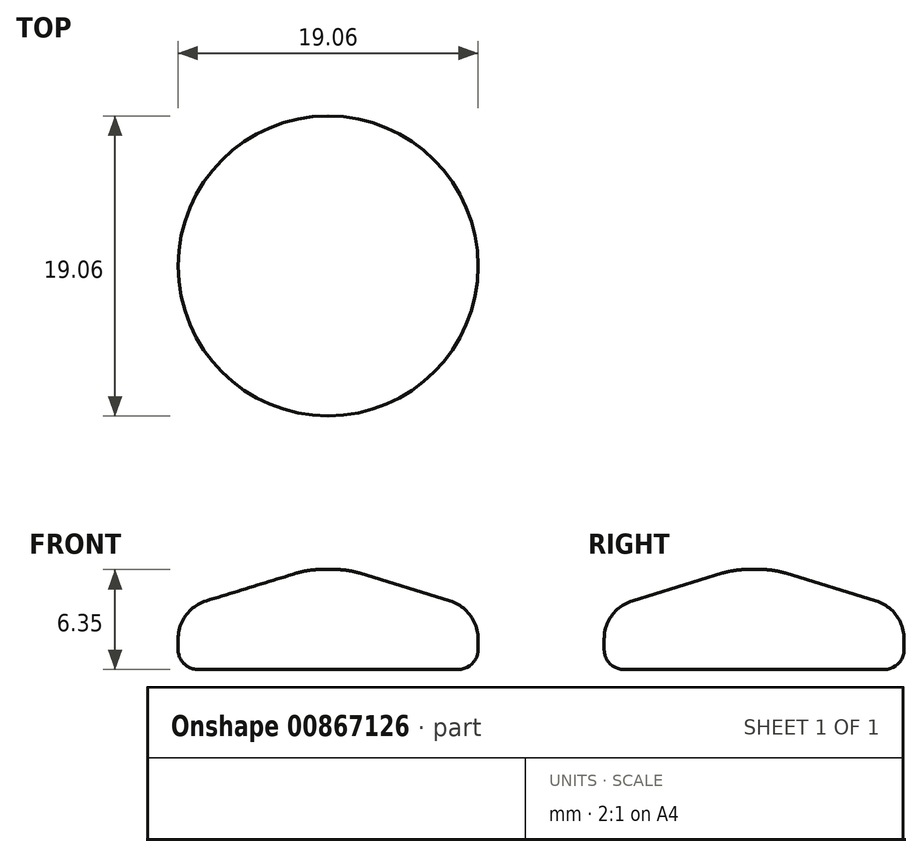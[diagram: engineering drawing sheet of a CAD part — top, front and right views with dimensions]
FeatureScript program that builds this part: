
annotation { "Feature Type Name" : "Feature", "Feature Type Description" : "" }
export const myFeature = defineFeature(function(context is Context, id is Id, definition is map)
    precondition{}
    {
        {
            var Q0;
            Q0=qCreatedBy(makeId("Front.planeOp"),FACE);
            var sketch = newSketch(context, id + "F0", { "sketchPlane" : qUnion([Q0])});
            skLineSegment(sketch, "E0", {"start": v(0, 0) * mm, "end": v(0, 6.35) * mm});
            skLineSegment(sketch, "E1", {"start": v(-9.53, 1.93) * mm, "end": v(-9.53, 1.27) * mm});
            skLineSegment(sketch, "E2", {"start": v(-8.26, 0) * mm, "end": v(0, 0) * mm});
            skLineSegment(sketch, "E3", {"start": v(-7.73, 4.36) * mm, "end": v(-2, 6.13) * mm});
            skLineSegment(sketch, "E4", {"start": v(-0.5, 6.35) * mm, "end": v(0, 6.35) * mm});
            skPoint(sketch, "E5.visualSharp", {"position": v(-9.53, 3.81) * mm});
            skArc(sketch, "E5.filletArc", {"start": v(-7.73, 4.36) * mm, "mid": v(-9.03, 3.44) * mm, "end": v(-9.53, 1.93) * mm});
            skPoint(sketch, "E6.visualSharp", {"position": v(-1.27, 6.35) * mm});
            skArc(sketch, "E6.filletArc", {"start": v(-0.5, 6.35) * mm, "mid": v(-1.26, 6.3) * mm, "end": v(-2, 6.13) * mm});
            skPoint(sketch, "E7.visualSharp", {"position": v(-9.53, 0) * mm});
            skArc(sketch, "E7.filletArc", {"start": v(-9.53, 1.27) * mm, "mid": v(-9.15, 0.37) * mm, "end": v(-8.26, 0) * mm});
            skSolve(sketch);
        }
        {
            var Q0;
            Q0=makeQuery(id+"F0.imprint","IMPRINT",FACE,{"disambiguationData":[TD([[makeQuery(id+"F0.imprint","IMPRINT",EDGE,{"derivedFrom":sQuery(id+"F0.wireOp",EDGE,"E0")}),1.0]])]});
            var Q1;
            Q1=sQuery(id+"F0.wireOp",EDGE,"E0");
            revolve(context, id + "F1", {"surfaceOperationType" : NewSurfaceOperationType.NEW, "entities" : qUnion([Q0]), "axis" : qUnion([Q1]), "revolveType" : RevolveType.FULL});
        }
    });
